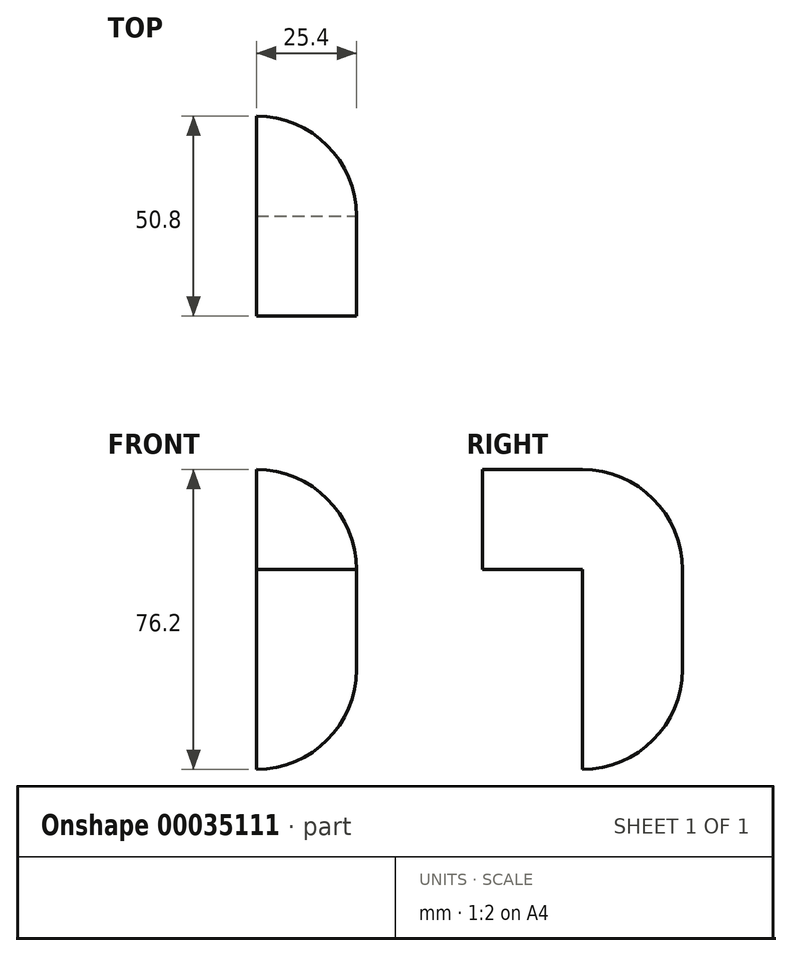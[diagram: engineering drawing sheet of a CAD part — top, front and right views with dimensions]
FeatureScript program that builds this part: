
annotation { "Feature Type Name" : "Feature", "Feature Type Description" : "" }
export const myFeature = defineFeature(function(context is Context, id is Id, definition is map)
    precondition{}
    {
        {
            var Q0;
            Q0=qCreatedBy(makeId("Top.planeOp"),FACE);
            var sketch = newSketch(context, id + "F0", { "sketchPlane" : qUnion([Q0])});
            skLineSegment(sketch, "E0", {"start": v(0, 0) * mm, "end": v(0, 25.4) * mm});
            skLineSegment(sketch, "E1", {"start": v(0, 25.4) * mm, "end": v(25.4, 25.4) * mm});
            skLineSegment(sketch, "E2", {"start": v(25.4, 25.4) * mm, "end": v(25.4, 0) * mm});
            skLineSegment(sketch, "E3", {"start": v(25.4, 0) * mm, "end": v(0, 0) * mm});
            skSolve(sketch);
        }
        {
            var Q0;
            Q0=makeQuery(id+"F0.imprint","IMPRINT",FACE,{"disambiguationData":[TD([[makeQuery(id+"F0.imprint","IMPRINT",EDGE,{"derivedFrom":sQuery(id+"F0.wireOp",EDGE,"E0")}),-1.0]])]});
            extrude(context, id + "F1", {"entities" : qUnion([Q0]), "depth" : 76.2 * mm});
        }
        {
            var Q0;
            Q0=makeQuery(id+"F1.opExtrude","SWEPT_FACE",FACE,{"disambiguationData":[OSD([sQuery(id+"F0.wireOp",EDGE,"E3")])]});
            var sketch = newSketch(context, id + "F2", { "sketchPlane" : qUnion([Q0])});
            skLineSegment(sketch, "E4", {"start": v(25.4, 76.2) * mm, "end": v(0, 76.2) * mm});
            skLineSegment(sketch, "E5", {"start": v(0, 76.2) * mm, "end": v(0, 50.8) * mm});
            skLineSegment(sketch, "E6", {"start": v(0, 50.8) * mm, "end": v(25.4, 50.8) * mm});
            skLineSegment(sketch, "E7", {"start": v(25.4, 50.8) * mm, "end": v(25.4, 76.2) * mm});
            skSolve(sketch);
        }
        {
            var Q0;
            Q0=makeQuery(id+"F2.imprint","IMPRINT",FACE,{"disambiguationData":[TD([[makeQuery(id+"F2.imprint","IMPRINT",EDGE,{"derivedFrom":sQuery(id+"F2.wireOp",EDGE,"E4")}),1.0]])]});
            extrude(context, id + "F3", {"entities" : qUnion([Q0]), "operationType" : NewBodyOperationType.ADD, "depth" : 25.4 * mm});
        }
        {
            var Q0;
            Q0=makeQuery(id+"F1.opExtrude","CAP_EDGE",EDGE,{"disambiguationData":[OSD([sQuery(id+"F0.wireOp",EDGE,"E1")])],"isStart":true});
            var Q1;
            Q1=makeQuery(id+"F1.opExtrude","CAP_EDGE",EDGE,{"disambiguationData":[OSD([sQuery(id+"F0.wireOp",EDGE,"E2")])],"isStart":true});
            var Q2;
            Q2=makeQuery(id+"F1.opExtrude","SWEPT_EDGE",EDGE,{"disambiguationData":[OSD([sQuery(id+"F0.wireOp",EDGE,"E1"),sQuery(id+"F0.wireOp",EDGE,"E2")])]});
            var Q3;
            Q3=makeQuery(id+"F3.boolean.opBoolean","MERGE",EDGE,{"derivedFrom":[makeQuery(id+"F1.opExtrude","CAP_EDGE",EDGE,{"disambiguationData":[OSD([sQuery(id+"F0.wireOp",EDGE,"E2")])],"isStart":false}),makeQuery(id+"F3.opExtrude","SWEPT_EDGE",EDGE,{"disambiguationData":[OSD([sQuery(id+"F2.wireOp",EDGE,"E4"),sQuery(id+"F2.wireOp",EDGE,"E7")])]})]});
            var Q4;
            Q4=makeQuery(id+"F1.opExtrude","CAP_EDGE",EDGE,{"disambiguationData":[OSD([sQuery(id+"F0.wireOp",EDGE,"E1")])],"isStart":false});
            fillet(context, id + "F4", {"entities" : qUnion([Q0, Q1, Q2, Q3, Q4]), "radius" : 25.4 * mm, "tangentPropagation" : true, "allowEdgeOverflow" : false});
        }
    });
